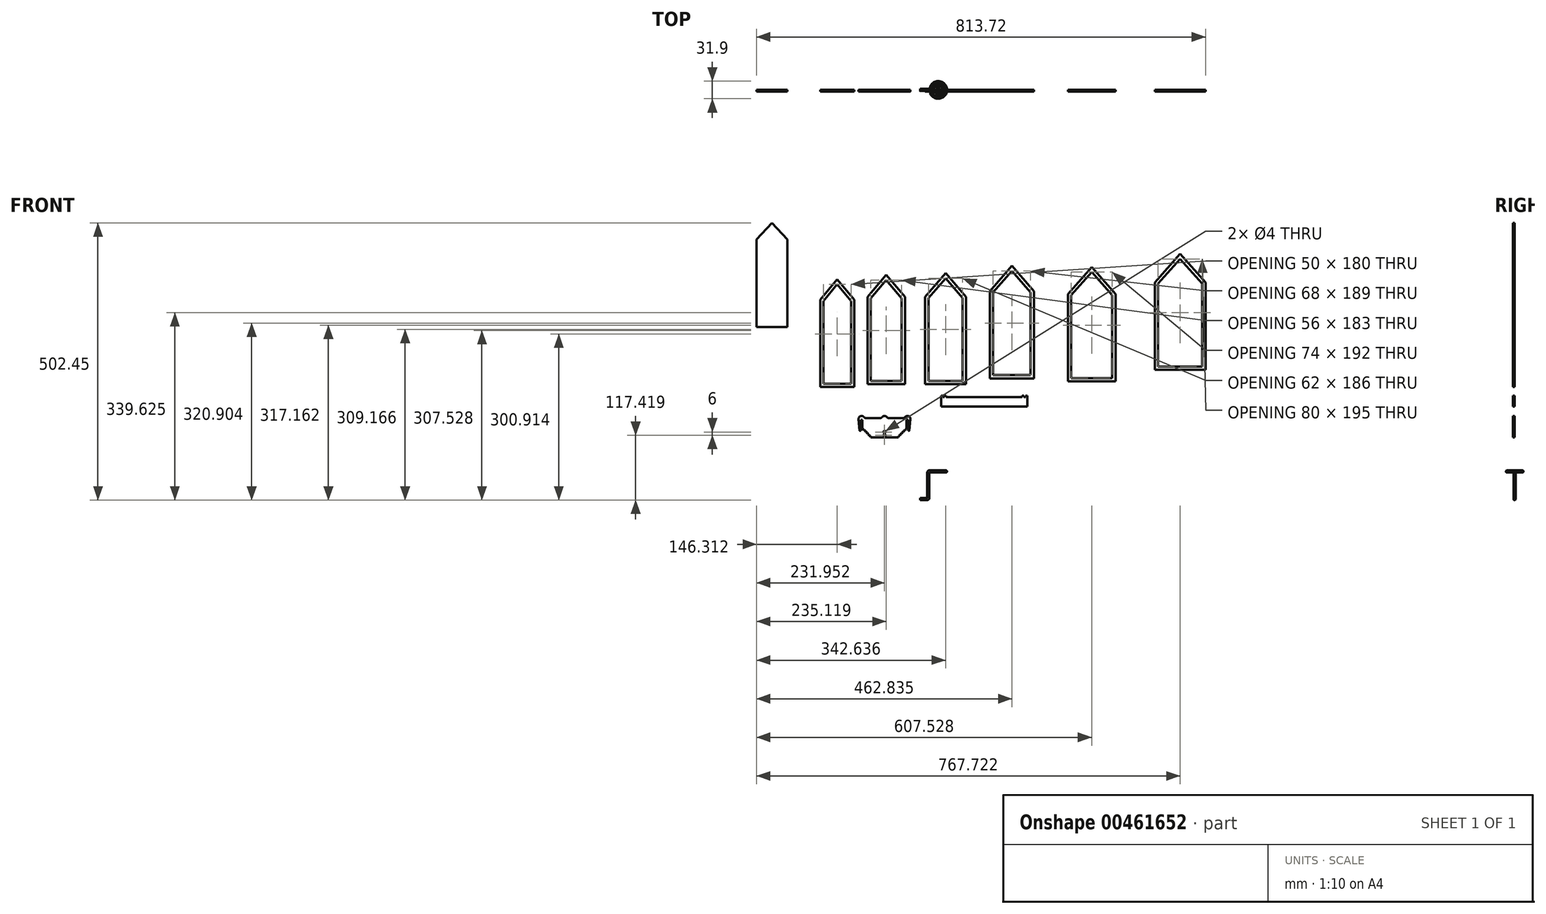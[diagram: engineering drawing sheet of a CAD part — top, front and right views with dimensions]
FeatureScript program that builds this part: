
annotation { "Feature Type Name" : "Feature", "Feature Type Description" : "" }
export const myFeature = defineFeature(function(context is Context, id is Id, definition is map)
    precondition{}
    {
        {
            var Q0;
            Q0=qCreatedBy(makeId("Front.planeOp"),FACE);
            var sketch = newSketch(context, id + "F0", { "sketchPlane" : qUnion([Q0])});
            skLineSegment(sketch, "E0.top", {"start": v(-296.35, 311.5) * mm, "end": v(-240.35, 311.5) * mm});
            skLineSegment(sketch, "E0.left", {"start": v(-296.35, 470.5) * mm, "end": v(-296.35, 311.5) * mm});
            skLineSegment(sketch, "E0.right", {"start": v(-240.35, 470.5) * mm, "end": v(-240.35, 311.5) * mm});
            skLineSegment(sketch, "E1", {"start": v(-64.4, 111.47) * mm, "end": v(-39.4, 111.47) * mm});
            skLineSegment(sketch, "E2", {"start": v(-39.4, 111.47) * mm, "end": v(-39.4, 114.47) * mm});
            skLineSegment(sketch, "E3", {"start": v(-39.4, 114.47) * mm, "end": v(-36.4, 114.47) * mm});
            skLineSegment(sketch, "E4", {"start": v(-36.4, 114.47) * mm, "end": v(-36.4, 117.47) * mm});
            skLineSegment(sketch, "E5", {"start": v(-36.4, 117.47) * mm, "end": v(-33.4, 117.47) * mm});
            skLineSegment(sketch, "E6", {"start": v(-33.4, 117.47) * mm, "end": v(-33.4, 120.47) * mm});
            skLineSegment(sketch, "E7", {"start": v(-33.4, 120.47) * mm, "end": v(-30.4, 120.47) * mm});
            skLineSegment(sketch, "E8", {"start": v(-30.4, 120.47) * mm, "end": v(-30.4, 123.47) * mm});
            skLineSegment(sketch, "E9", {"start": v(-30.4, 123.47) * mm, "end": v(-27.4, 123.47) * mm});
            skLineSegment(sketch, "E10", {"start": v(-27.4, 123.47) * mm, "end": v(-27.4, 126.47) * mm});
            skLineSegment(sketch, "E11", {"start": v(-27.4, 126.47) * mm, "end": v(-24.4, 126.47) * mm});
            skLineSegment(sketch, "E12", {"start": v(-24.4, 126.47) * mm, "end": v(-24.4, 143.47) * mm});
            skLineSegment(sketch, "E13", {"start": v(-31.22, 146.47) * mm, "end": v(-56.07, 146.47) * mm});
            skLineSegment(sketch, "E14", {"start": v(-64.4, 111.47) * mm, "end": v(-64.4, 113.47) * mm});
            skLineSegment(sketch, "E15", {"start": v(-21.4, 143.47) * mm, "end": v(-24.4, 143.47) * mm});
            skLineSegment(sketch, "E16", {"start": v(-21.4, 143.47) * mm, "end": v(-21.4, 123.47) * mm});
            skLineSegment(sketch, "E17", {"start": v(-21.4, 123.47) * mm, "end": v(-19.85, 123.47) * mm});
            skArc(sketch, "E18", {"start": v(-17.36, 144.43) * mm, "mid": v(-20.84, 150.13) * mm, "end": v(-27.28, 148.4) * mm});
            skPoint(sketch, "E18.centerSnap0", {"position": v(-22.9, 146.47) * mm});
            skPoint(sketch, "E18.centerSnap1", {"position": v(-21.4, 144.97) * mm});
            skLineSegment(sketch, "E19", {"start": v(-19.35, 123.92) * mm, "end": v(-17.36, 144.43) * mm});
            skPoint(sketch, "E20.start.orphan", {"position": v(-24.4, 146.47) * mm});
            skPoint(sketch, "E21.orphan", {"position": v(-21.4, 146.47) * mm});
            skPoint(sketch, "E22.visualSharp", {"position": v(-28.25, 146.47) * mm});
            skArc(sketch, "E22.filletArc", {"start": v(-31.22, 146.47) * mm, "mid": v(-29.03, 146.97) * mm, "end": v(-27.28, 148.4) * mm});
            skPoint(sketch, "E23.visualSharp", {"position": v(-19.4, 123.47) * mm});
            skArc(sketch, "E23.filletArc", {"start": v(-19.85, 123.47) * mm, "mid": v(-19.52, 123.6) * mm, "end": v(-19.35, 123.92) * mm});
            skArc(sketch, "E24", {"start": v(-64.4, 113.47) * mm, "mid": v(-62.4, 115.47) * mm, "end": v(-64.4, 117.47) * mm});
            skArc(sketch, "E25", {"start": v(-64.4, 119.47) * mm, "mid": v(-62.4, 121.47) * mm, "end": v(-64.4, 123.47) * mm});
            skLineSegment(sketch, "E26.bottom", {"start": v(41.16, 184.45) * mm, "end": v(44.16, 184.45) * mm});
            skLineSegment(sketch, "E26.top", {"start": v(38.16, 167.45) * mm, "end": v(194.16, 167.45) * mm});
            skLineSegment(sketch, "E26.left", {"start": v(38.16, 184.45) * mm, "end": v(38.16, 167.45) * mm});
            skLineSegment(sketch, "E26.right", {"start": v(194.16, 184.45) * mm, "end": v(194.16, 167.45) * mm});
            skArc(sketch, "E27", {"start": v(-60.02, 148.4) * mm, "mid": v(-61.96, 149.97) * mm, "end": v(-64.4, 150.53) * mm});
            skLineSegment(sketch, "E28", {"start": v(-64.4, 146.47) * mm, "end": v(-64.4, 150.53) * mm});
            skLineSegment(sketch, "E29.trimOffspring", {"start": v(-64.4, 123.47) * mm, "end": v(-64.4, 146.47) * mm});
            skLineSegment(sketch, "E30.trimOffspring", {"start": v(-64.4, 117.47) * mm, "end": v(-64.4, 119.47) * mm});
            skPoint(sketch, "E31.visualSharp", {"position": v(-59.04, 146.47) * mm});
            skArc(sketch, "E31.filletArc", {"start": v(-60.02, 148.4) * mm, "mid": v(-58.27, 146.97) * mm, "end": v(-56.07, 146.47) * mm});
            skArc(sketch, "E32.MirrorCS", {"start": v(-108.94, 123.47) * mm, "mid": v(-109.28, 123.6) * mm, "end": v(-109.44, 123.92) * mm});
            skLineSegment(sketch, "E33.MirrorCS", {"start": v(-101.4, 123.47) * mm, "end": v(-101.4, 126.47) * mm});
            skLineSegment(sketch, "E34.MirrorCS", {"start": v(-98.4, 120.47) * mm, "end": v(-98.4, 123.47) * mm});
            skLineSegment(sketch, "E35.MirrorCS", {"start": v(-95.4, 117.47) * mm, "end": v(-95.4, 120.47) * mm});
            skLineSegment(sketch, "E36.MirrorCS", {"start": v(-92.4, 114.47) * mm, "end": v(-92.4, 117.47) * mm});
            skLineSegment(sketch, "E37.MirrorCS", {"start": v(-107.4, 123.47) * mm, "end": v(-108.94, 123.47) * mm});
            skLineSegment(sketch, "E38.MirrorCS", {"start": v(-89.4, 111.47) * mm, "end": v(-89.4, 114.47) * mm});
            skLineSegment(sketch, "E39.MirrorCS", {"start": v(-98.4, 123.47) * mm, "end": v(-101.4, 123.47) * mm});
            skLineSegment(sketch, "E40.MirrorCS", {"start": v(-95.4, 120.47) * mm, "end": v(-98.4, 120.47) * mm});
            skLineSegment(sketch, "E41.MirrorCS", {"start": v(-92.4, 117.47) * mm, "end": v(-95.4, 117.47) * mm});
            skArc(sketch, "E42.MirrorCS", {"start": v(-68.78, 148.4) * mm, "mid": v(-70.53, 146.97) * mm, "end": v(-72.72, 146.47) * mm});
            skLineSegment(sketch, "E43.MirrorCS", {"start": v(-89.4, 114.47) * mm, "end": v(-92.4, 114.47) * mm});
            skLineSegment(sketch, "E44.MirrorCS", {"start": v(-101.4, 126.47) * mm, "end": v(-104.4, 126.47) * mm});
            skLineSegment(sketch, "E45.MirrorCS", {"start": v(-104.4, 126.47) * mm, "end": v(-104.4, 143.47) * mm});
            skLineSegment(sketch, "E46.MirrorCS", {"start": v(-97.57, 146.47) * mm, "end": v(-72.72, 146.47) * mm});
            skLineSegment(sketch, "E47.MirrorCS", {"start": v(-107.4, 143.47) * mm, "end": v(-104.4, 143.47) * mm});
            skLineSegment(sketch, "E48.MirrorCS", {"start": v(-107.4, 143.47) * mm, "end": v(-107.4, 123.47) * mm});
            skArc(sketch, "E49.MirrorCS", {"start": v(-68.78, 148.4) * mm, "mid": v(-66.84, 149.97) * mm, "end": v(-64.4, 150.53) * mm});
            skPoint(sketch, "E50.MirrorP", {"position": v(-109.4, 123.47) * mm});
            skPoint(sketch, "E51.MirrorP", {"position": v(-69.75, 146.47) * mm});
            skPoint(sketch, "E52.MirrorP", {"position": v(-100.54, 146.47) * mm});
            skArc(sketch, "E53.MirrorCS", {"start": v(-111.43, 144.43) * mm, "mid": v(-107.96, 150.13) * mm, "end": v(-101.52, 148.4) * mm});
            skLineSegment(sketch, "E54.MirrorCS", {"start": v(-109.44, 123.92) * mm, "end": v(-111.43, 144.43) * mm});
            skLineSegment(sketch, "E55.MirrorCS", {"start": v(-64.4, 111.47) * mm, "end": v(-89.4, 111.47) * mm});
            skArc(sketch, "E56.MirrorCS", {"start": v(-97.57, 146.47) * mm, "mid": v(-99.77, 146.97) * mm, "end": v(-101.52, 148.4) * mm});
            skPoint(sketch, "E57.MirrorP", {"position": v(-105.9, 146.47) * mm});
            skPoint(sketch, "E58.MirrorP", {"position": v(-107.4, 144.97) * mm});
            skArc(sketch, "E59.MirrorCS", {"start": v(-64.4, 113.47) * mm, "mid": v(-66.4, 115.47) * mm, "end": v(-64.4, 117.47) * mm});
            skPoint(sketch, "E60.MirrorP", {"position": v(-104.4, 146.47) * mm});
            skArc(sketch, "E61.MirrorCS", {"start": v(-64.4, 119.47) * mm, "mid": v(-66.4, 121.47) * mm, "end": v(-64.4, 123.47) * mm});
            skPoint(sketch, "E62.MirrorP", {"position": v(-107.4, 146.47) * mm});
            skLineSegment(sketch, "E63.top", {"start": v(-175.04, 208.96) * mm, "end": v(-125.04, 208.96) * mm});
            skLineSegment(sketch, "E63.left", {"start": v(-175.04, 358.96) * mm, "end": v(-175.04, 208.96) * mm});
            skLineSegment(sketch, "E63.right", {"start": v(-125.04, 358.96) * mm, "end": v(-125.04, 208.96) * mm});
            skLineSegment(sketch, "E64", {"start": v(-150.04, 388.96) * mm, "end": v(-175.04, 358.96) * mm});
            skLineSegment(sketch, "E65", {"start": v(-150.04, 388.96) * mm, "end": v(-125.04, 358.96) * mm});
            skPoint(sketch, "E66.start.orphan", {"position": v(-150.04, 358.96) * mm});
            skLineSegment(sketch, "E67.top", {"start": v(-89.23, 214.08) * mm, "end": v(-33.23, 214.08) * mm});
            skLineSegment(sketch, "E67.left", {"start": v(-89.23, 364.08) * mm, "end": v(-89.23, 214.08) * mm});
            skLineSegment(sketch, "E67.right", {"start": v(-33.23, 364.08) * mm, "end": v(-33.23, 214.08) * mm});
            skLineSegment(sketch, "E68", {"start": v(-61.23, 397.08) * mm, "end": v(-89.23, 364.08) * mm});
            skLineSegment(sketch, "E69", {"start": v(-61.23, 397.08) * mm, "end": v(-33.23, 364.08) * mm});
            skPoint(sketch, "E70.start.orphan", {"position": v(-64.23, 364.08) * mm});
            skLineSegment(sketch, "E71.top", {"start": v(15.29, 214.22) * mm, "end": v(77.29, 214.22) * mm});
            skLineSegment(sketch, "E71.left", {"start": v(15.29, 364.22) * mm, "end": v(15.29, 214.22) * mm});
            skLineSegment(sketch, "E71.right", {"start": v(77.29, 364.22) * mm, "end": v(77.29, 214.22) * mm});
            skLineSegment(sketch, "E72", {"start": v(46.29, 400.22) * mm, "end": v(15.29, 364.22) * mm});
            skLineSegment(sketch, "E73", {"start": v(46.29, 400.22) * mm, "end": v(77.29, 364.22) * mm});
            skPoint(sketch, "E74.start.orphan", {"position": v(40.29, 364.22) * mm});
            skLineSegment(sketch, "E75.top", {"start": v(132.48, 224.45) * mm, "end": v(200.48, 224.45) * mm});
            skLineSegment(sketch, "E75.left", {"start": v(132.48, 374.45) * mm, "end": v(132.48, 224.45) * mm});
            skLineSegment(sketch, "E75.right", {"start": v(200.48, 374.45) * mm, "end": v(200.48, 224.45) * mm});
            skLineSegment(sketch, "E76", {"start": v(166.48, 413.45) * mm, "end": v(132.48, 374.45) * mm});
            skLineSegment(sketch, "E77", {"start": v(166.48, 413.45) * mm, "end": v(200.48, 374.45) * mm});
            skPoint(sketch, "E78.start.orphan", {"position": v(157.48, 374.45) * mm});
            skLineSegment(sketch, "E79.top", {"start": v(274.18, 219.21) * mm, "end": v(348.18, 219.21) * mm});
            skLineSegment(sketch, "E79.left", {"start": v(274.18, 369.21) * mm, "end": v(274.18, 219.21) * mm});
            skLineSegment(sketch, "E79.right", {"start": v(348.18, 369.21) * mm, "end": v(348.18, 219.21) * mm});
            skLineSegment(sketch, "E80", {"start": v(311.18, 411.21) * mm, "end": v(274.18, 369.21) * mm});
            skLineSegment(sketch, "E81", {"start": v(311.18, 411.21) * mm, "end": v(348.18, 369.21) * mm});
            skPoint(sketch, "E82.start.orphan", {"position": v(299.18, 369.21) * mm});
            skLineSegment(sketch, "E83.top", {"start": v(431.37, 240.18) * mm, "end": v(511.37, 240.18) * mm});
            skLineSegment(sketch, "E83.left", {"start": v(431.37, 390.18) * mm, "end": v(431.37, 240.18) * mm});
            skLineSegment(sketch, "E83.right", {"start": v(511.37, 390.18) * mm, "end": v(511.37, 240.18) * mm});
            skLineSegment(sketch, "E84", {"start": v(471.37, 435.18) * mm, "end": v(431.37, 390.18) * mm});
            skLineSegment(sketch, "E85", {"start": v(471.37, 435.18) * mm, "end": v(511.37, 390.18) * mm});
            skPoint(sketch, "E86.start.orphan", {"position": v(456.37, 390.18) * mm});
            skLineSegment(sketch, "E87.0", {"start": v(-119.04, 361.14) * mm, "end": v(-119.04, 202.96) * mm});
            skLineSegment(sketch, "E87.1", {"start": v(-150.04, 398.34) * mm, "end": v(-119.04, 361.14) * mm});
            skLineSegment(sketch, "E87.2", {"start": v(-181.04, 202.96) * mm, "end": v(-119.04, 202.96) * mm});
            skLineSegment(sketch, "E87.3", {"start": v(-181.04, 361.14) * mm, "end": v(-181.04, 202.96) * mm});
            skLineSegment(sketch, "E87.4", {"start": v(-150.04, 398.34) * mm, "end": v(-181.04, 361.14) * mm});
            skLineSegment(sketch, "E88.0", {"start": v(-95.23, 208.08) * mm, "end": v(-27.23, 208.08) * mm});
            skLineSegment(sketch, "E88.1", {"start": v(-95.23, 366.28) * mm, "end": v(-95.23, 208.08) * mm});
            skLineSegment(sketch, "E88.2", {"start": v(-27.23, 366.28) * mm, "end": v(-27.23, 208.08) * mm});
            skLineSegment(sketch, "E88.3", {"start": v(-61.23, 406.35) * mm, "end": v(-27.23, 366.28) * mm});
            skLineSegment(sketch, "E88.4", {"start": v(-61.23, 406.35) * mm, "end": v(-95.23, 366.28) * mm});
            skLineSegment(sketch, "E89.0", {"start": v(83.29, 366.44) * mm, "end": v(83.29, 208.22) * mm});
            skLineSegment(sketch, "E89.1", {"start": v(46.29, 409.41) * mm, "end": v(83.29, 366.44) * mm});
            skLineSegment(sketch, "E89.2", {"start": v(9.29, 208.22) * mm, "end": v(83.29, 208.22) * mm});
            skLineSegment(sketch, "E89.3", {"start": v(9.29, 366.44) * mm, "end": v(9.29, 208.22) * mm});
            skLineSegment(sketch, "E89.4", {"start": v(46.29, 409.41) * mm, "end": v(9.29, 366.44) * mm});
            skLineSegment(sketch, "E90.0", {"start": v(206.48, 376.7) * mm, "end": v(206.48, 218.45) * mm});
            skLineSegment(sketch, "E90.1", {"start": v(166.48, 422.58) * mm, "end": v(206.48, 376.7) * mm});
            skLineSegment(sketch, "E90.2", {"start": v(126.48, 218.45) * mm, "end": v(206.48, 218.45) * mm});
            skLineSegment(sketch, "E90.3", {"start": v(126.48, 376.7) * mm, "end": v(126.48, 218.45) * mm});
            skLineSegment(sketch, "E90.4", {"start": v(166.48, 422.58) * mm, "end": v(126.48, 376.7) * mm});
            skLineSegment(sketch, "E91.0", {"start": v(268.18, 213.21) * mm, "end": v(354.18, 213.21) * mm});
            skLineSegment(sketch, "E91.1", {"start": v(268.18, 371.48) * mm, "end": v(268.18, 213.21) * mm});
            skLineSegment(sketch, "E91.2", {"start": v(354.18, 371.48) * mm, "end": v(354.18, 213.21) * mm});
            skLineSegment(sketch, "E91.3", {"start": v(311.18, 420.29) * mm, "end": v(354.18, 371.48) * mm});
            skLineSegment(sketch, "E91.4", {"start": v(311.18, 420.29) * mm, "end": v(268.18, 371.48) * mm});
            skLineSegment(sketch, "E92.0", {"start": v(425.37, 234.18) * mm, "end": v(517.37, 234.18) * mm});
            skLineSegment(sketch, "E92.1", {"start": v(425.37, 392.46) * mm, "end": v(425.37, 234.18) * mm});
            skLineSegment(sketch, "E92.2", {"start": v(517.37, 392.46) * mm, "end": v(517.37, 234.18) * mm});
            skLineSegment(sketch, "E92.3", {"start": v(471.37, 444.2) * mm, "end": v(517.37, 392.46) * mm});
            skLineSegment(sketch, "E92.4", {"start": v(471.37, 444.2) * mm, "end": v(425.37, 392.46) * mm});
            skLineSegment(sketch, "E93", {"start": v(-296.35, 470.5) * mm, "end": v(-268.35, 500.5) * mm});
            skPoint(sketch, "E93.endSnap0", {"position": v(-268.35, 470.5) * mm});
            skLineSegment(sketch, "E94", {"start": v(-268.35, 500.5) * mm, "end": v(-240.35, 470.5) * mm});
            skLineSegment(sketch, "E95.top", {"start": v(38.16, 187.45) * mm, "end": v(41.16, 187.45) * mm});
            skLineSegment(sketch, "E95.left", {"start": v(38.16, 184.45) * mm, "end": v(38.16, 187.45) * mm});
            skLineSegment(sketch, "E95.right", {"start": v(41.16, 184.45) * mm, "end": v(41.16, 187.45) * mm});
            skLineSegment(sketch, "E96.top", {"start": v(194.16, 187.45) * mm, "end": v(191.16, 187.45) * mm});
            skLineSegment(sketch, "E96.left", {"start": v(194.16, 184.45) * mm, "end": v(194.16, 187.45) * mm});
            skLineSegment(sketch, "E96.right", {"start": v(191.16, 184.45) * mm, "end": v(191.16, 187.45) * mm});
            skLineSegment(sketch, "E97.top", {"start": v(188.16, 187.45) * mm, "end": v(185.16, 187.45) * mm});
            skLineSegment(sketch, "E97.left", {"start": v(188.16, 184.45) * mm, "end": v(188.16, 187.45) * mm});
            skLineSegment(sketch, "E97.right", {"start": v(185.16, 184.45) * mm, "end": v(185.16, 187.45) * mm});
            skLineSegment(sketch, "E98.top", {"start": v(44.16, 187.45) * mm, "end": v(47.16, 187.45) * mm});
            skLineSegment(sketch, "E98.left", {"start": v(44.16, 184.45) * mm, "end": v(44.16, 187.45) * mm});
            skLineSegment(sketch, "E98.right", {"start": v(47.16, 184.45) * mm, "end": v(47.16, 187.45) * mm});
            skLineSegment(sketch, "E99.trimOffspring", {"start": v(188.16, 184.45) * mm, "end": v(191.16, 184.45) * mm});
            skLineSegment(sketch, "E100.trimOffspring", {"start": v(47.16, 184.45) * mm, "end": v(185.16, 184.45) * mm});
            skSolve(sketch);
        }
        {
            var Q0;
            Q0 = qSketchRegion(id + "F0", true);
            extrude(context, id + "F1", {"entities" : qUnion([Q0]), "depth" : 3 * mm, "offsetDistance" : 25 * mm});
        }
        {
            var Q0;
            Q0=qCreatedBy(makeId("Front.planeOp"),FACE);
            var sketch = newSketch(context, id + "F2", { "sketchPlane" : qUnion([Q0])});
            skLineSegment(sketch, "E101", {"start": v(0, 0) * mm, "end": v(13, 0) * mm});
            skLineSegment(sketch, "E102", {"start": v(15, 2) * mm, "end": v(15, 48) * mm});
            skLineSegment(sketch, "E103", {"start": v(17, 50) * mm, "end": v(17, 50) * mm});
            skPoint(sketch, "E104.visualSharp", {"position": v(15, 50) * mm});
            skArc(sketch, "E104.filletArc", {"start": v(17, 50) * mm, "mid": v(15.59, 49.41) * mm, "end": v(15, 48) * mm});
            skPoint(sketch, "E105.visualSharp", {"position": v(15, 0) * mm});
            skArc(sketch, "E105.filletArc", {"start": v(13, 0) * mm, "mid": v(14.41, 0.59) * mm, "end": v(15, 2) * mm});
            skSolve(sketch);
        }
        {
            var Q0;
            Q0=qCreatedBy(makeId("Right.planeOp"),FACE);
            var sketch = newSketch(context, id + "F3", { "sketchPlane" : qUnion([Q0])});
            skCircle(sketch, "E106", {"center": v(0, 0) * mm, "radius": 1.95 * mm});
            skSolve(sketch);
        }
        {
            var Q0;
            Q0=qCreatedBy(makeId("Top.planeOp"),FACE);
            cPlane(context, id + "F4", {"entities" : qUnion([Q0]), "cplaneType" : CPlaneType.OFFSET, "offset" : 50 * mm, "width" : 150 * mm, "height" : 150 * mm});
        }
        {
            var Q0;
            Q0=qCreatedBy(id+"F4.planeOp",FACE);
            var sketch = newSketch(context, id + "F5", { "sketchPlane" : qUnion([Q0])});
            skArc(sketch, "E107", {"start": v(27.12, -8.09) * mm, "mid": v(41.62, 5.06) * mm, "end": v(23.07, -1.19) * mm});
            skArc(sketch, "E108", {"start": v(20.42, -6.14) * mm, "mid": v(46.81, 2.3) * mm, "end": v(19.1, 1.75) * mm});
            skArc(sketch, "E109", {"start": v(34.9, -5.7) * mm, "mid": v(35.37, 5.51) * mm, "end": v(27.56, -2.54) * mm});
            skCircle(sketch, "E110", {"center": v(33, 0) * mm, "radius": 2 * mm});
            skPoint(sketch, "E111", {"position": v(19.57, -3.96) * mm});
            skPoint(sketch, "E112", {"position": v(25.28, -6.36) * mm});
            skPoint(sketch, "E113", {"position": v(31.8, -5.88) * mm});
            skLineSegment(sketch, "E114", {"start": v(21.65, -3.35) * mm, "end": v(21.65, -3.35) * mm});
            skLineSegment(sketch, "E115", {"start": v(27.02, -4.93) * mm, "end": v(27.02, -4.93) * mm});
            skLineSegment(sketch, "E116", {"start": v(32.3, -3.4) * mm, "end": v(33, 0) * mm});
            skPoint(sketch, "E117", {"position": v(19, 0) * mm});
            skPoint(sketch, "E118", {"position": v(23.4, -2.83) * mm});
            skPoint(sketch, "E119", {"position": v(28.37, -3.82) * mm});
            skArc(sketch, "E120.filletArc", {"start": v(21.65, -3.35) * mm, "mid": v(20.39, -4.46) * mm, "end": v(20.42, -6.14) * mm});
            skArc(sketch, "E121.filletArc", {"start": v(21.65, -3.35) * mm, "mid": v(22.76, -2.53) * mm, "end": v(23.07, -1.19) * mm});
            skArc(sketch, "E122.filletArc", {"start": v(27.02, -4.93) * mm, "mid": v(26.3, -6.53) * mm, "end": v(27.12, -8.09) * mm});
            skArc(sketch, "E123.filletArc", {"start": v(27.02, -4.93) * mm, "mid": v(27.7, -3.82) * mm, "end": v(27.56, -2.54) * mm});
            skArc(sketch, "E124.filletArc", {"start": v(32.3, -3.4) * mm, "mid": v(32.94, -5.3) * mm, "end": v(34.9, -5.7) * mm});
            skLineSegment(sketch, "E125", {"start": v(17.13, 0) * mm, "end": v(17, 0) * mm});
            skArc(sketch, "E126.filletArc", {"start": v(17.13, 0) * mm, "mid": v(18.45, 0.5) * mm, "end": v(19.1, 1.75) * mm});
            skSolve(sketch);
        }
        {
            var Q0;
            Q0=makeQuery(id+"F3.imprint","IMPRINT",FACE,{"disambiguationData":[TD([[makeQuery(id+"F3.imprint","IMPRINT",EDGE,{"derivedFrom":sQuery(id+"F3.wireOp",EDGE,"E106")}),1.0]])]});
            var Q1;
            Q1=sQuery(id+"F2.wireOp",EDGE,"E101");
            var Q2;
            Q2=sQuery(id+"F2.wireOp",EDGE,"E105.filletArc");
            var Q3;
            Q3=sQuery(id+"F2.wireOp",EDGE,"E102");
            var Q4;
            Q4=sQuery(id+"F2.wireOp",EDGE,"E104.filletArc");
            var Q5;
            Q5=sQuery(id+"F2.wireOp",EDGE,"E103");
            var Q6;
            Q6=sQuery(id+"F5.wireOp",EDGE,"E108");
            var Q7;
            Q7=sQuery(id+"F5.wireOp",EDGE,"E120.filletArc");
            var Q8;
            Q8=sQuery(id+"F5.wireOp",EDGE,"E121.filletArc");
            var Q9;
            Q9=sQuery(id+"F5.wireOp",EDGE,"E107");
            var Q10;
            Q10=sQuery(id+"F5.wireOp",EDGE,"E122.filletArc");
            var Q11;
            Q11=sQuery(id+"F5.wireOp",EDGE,"E123.filletArc");
            var Q12;
            Q12=sQuery(id+"F5.wireOp",EDGE,"E109");
            var Q13;
            Q13=sQuery(id+"F5.wireOp",EDGE,"E124.filletArc");
            var Q14;
            Q14=sQuery(id+"F5.wireOp",EDGE,"E116");
            var Q15;
            Q15=sQuery(id+"F5.wireOp",EDGE,"E126.filletArc");
            var Q16;
            Q16=sQuery(id+"F5.wireOp",EDGE,"E125");
            sweep(context, id + "F6", {"profiles" : qUnion([Q0]), "path" : qUnion([Q1, Q2, Q3, Q4, Q5, Q6, Q7, Q8, Q9, Q10, Q11, Q12, Q13, Q14, Q15, Q16])});
        }
    });
